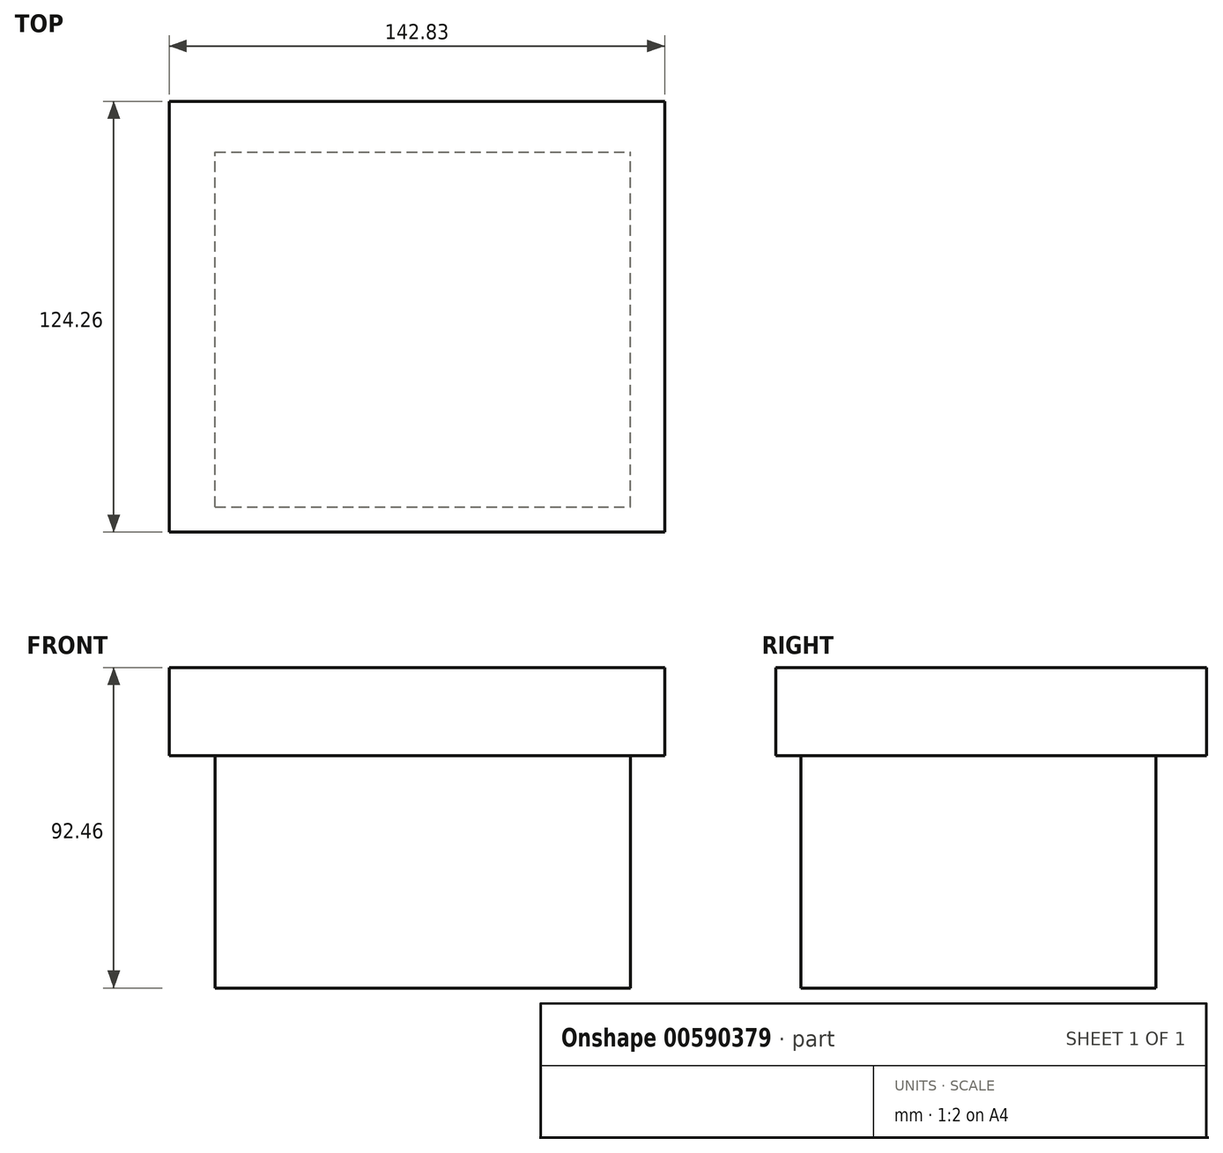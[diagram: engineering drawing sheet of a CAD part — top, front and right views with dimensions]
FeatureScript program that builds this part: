
annotation { "Feature Type Name" : "Feature", "Feature Type Description" : "" }
export const myFeature = defineFeature(function(context is Context, id is Id, definition is map)
    precondition{}
    {
        {
            var Q0;
            Q0=qCreatedBy(makeId("Top.planeOp"),FACE);
            var sketch = newSketch(context, id + "F0", { "sketchPlane" : qUnion([Q0])});
            skLineSegment(sketch, "E0.bottom", {"start": v(-88.4, -54.03) * mm, "end": v(54.42, -54.03) * mm});
            skLineSegment(sketch, "E0.top", {"start": v(-88.4, 70.23) * mm, "end": v(54.42, 70.23) * mm});
            skLineSegment(sketch, "E0.left", {"start": v(-88.4, -54.03) * mm, "end": v(-88.4, 70.23) * mm});
            skLineSegment(sketch, "E0.right", {"start": v(54.42, -54.03) * mm, "end": v(54.42, 70.23) * mm});
            skLineSegment(sketch, "E1.bottom", {"start": v(54.42, 70.23) * mm, "end": v(105.78, 70.23) * mm});
            skLineSegment(sketch, "E1.top", {"start": v(54.42, 70.23) * mm, "end": v(105.78, 70.23) * mm});
            skLineSegment(sketch, "E1.left", {"start": v(54.42, 70.23) * mm, "end": v(54.42, 70.23) * mm});
            skLineSegment(sketch, "E1.right", {"start": v(105.78, 70.23) * mm, "end": v(105.78, 70.23) * mm});
            skSolve(sketch);
        }
        {
            var Q0;
            Q0=makeQuery(id+"F0.imprint","IMPRINT",FACE,{"disambiguationData":[TD([[makeQuery(id+"F0.imprint","IMPRINT",EDGE,{"derivedFrom":sQuery(id+"F0.wireOp",EDGE,"E0.bottom")}),1.0]])]});
            extrude(context, id + "F1", {"entities" : qUnion([Q0]), "depth" : 25.4 * mm, "offsetDistance" : 25.4 * mm});
        }
        {
            var Q0;
            Q0=makeQuery(id+"F1.opExtrude","CAP_FACE",FACE,{"disambiguationData":[OSD([sQuery(id+"F0.wireOp",EDGE,"E0.bottom"),sQuery(id+"F0.wireOp",EDGE,"E0.top"),sQuery(id+"F0.wireOp",EDGE,"E0.left"),sQuery(id+"F0.wireOp",EDGE,"E0.right")])],"isStart":true});
            var sketch = newSketch(context, id + "F2", { "sketchPlane" : qUnion([Q0])});
            skLineSegment(sketch, "E2.bottom", {"start": v(-75.15, 46.69) * mm, "end": v(44.54, 46.69) * mm});
            skLineSegment(sketch, "E2.top", {"start": v(-75.15, -55.6) * mm, "end": v(44.54, -55.6) * mm});
            skLineSegment(sketch, "E2.left", {"start": v(-75.15, 46.69) * mm, "end": v(-75.15, -55.6) * mm});
            skLineSegment(sketch, "E2.right", {"start": v(44.54, 46.69) * mm, "end": v(44.54, -55.6) * mm});
            skSolve(sketch);
        }
        {
            var Q0;
            Q0=makeQuery(id+"F2.imprint","IMPRINT",FACE,{"disambiguationData":[TD([[makeQuery(id+"F2.imprint","IMPRINT",EDGE,{"derivedFrom":sQuery(id+"F2.wireOp",EDGE,"E2.bottom")}),-1.0]])]});
            extrude(context, id + "F3", {"entities" : qUnion([Q0]), "operationType" : NewBodyOperationType.ADD, "depth" : 67.06 * mm, "offsetDistance" : 25.4 * mm});
        }
        {
            var Q0;
            Q0=makeQuery(id+"F3.opExtrude","SWEPT_FACE",FACE,{"disambiguationData":[OSD([sQuery(id+"F2.wireOp",EDGE,"E2.bottom")])]});
            var sketch = newSketch(context, id + "F4", { "sketchPlane" : qUnion([Q0])});
            skCircle(sketch, "E3", {"center": v(-68.03, -67.06) * mm, "radius": 12.56 * mm});
            skCircle(sketch, "E4", {"center": v(37.58, -67.06) * mm, "radius": 12.32 * mm});
            skSolve(sketch);
        }
        {
            var Q0;
            Q0=sQuery(id+"F4.wireOp",EDGE,"E3");
            var Q1;
            Q1=sQuery(id+"F4.wireOp",EDGE,"E4");
            extrude(context, id + "F5", {"bodyType" : ToolBodyType.SURFACE, "surfaceEntities" : qUnion([Q0, Q1]), "depth" : 14.22 * mm, "offsetDistance" : 25.4 * mm});
        }
    });
